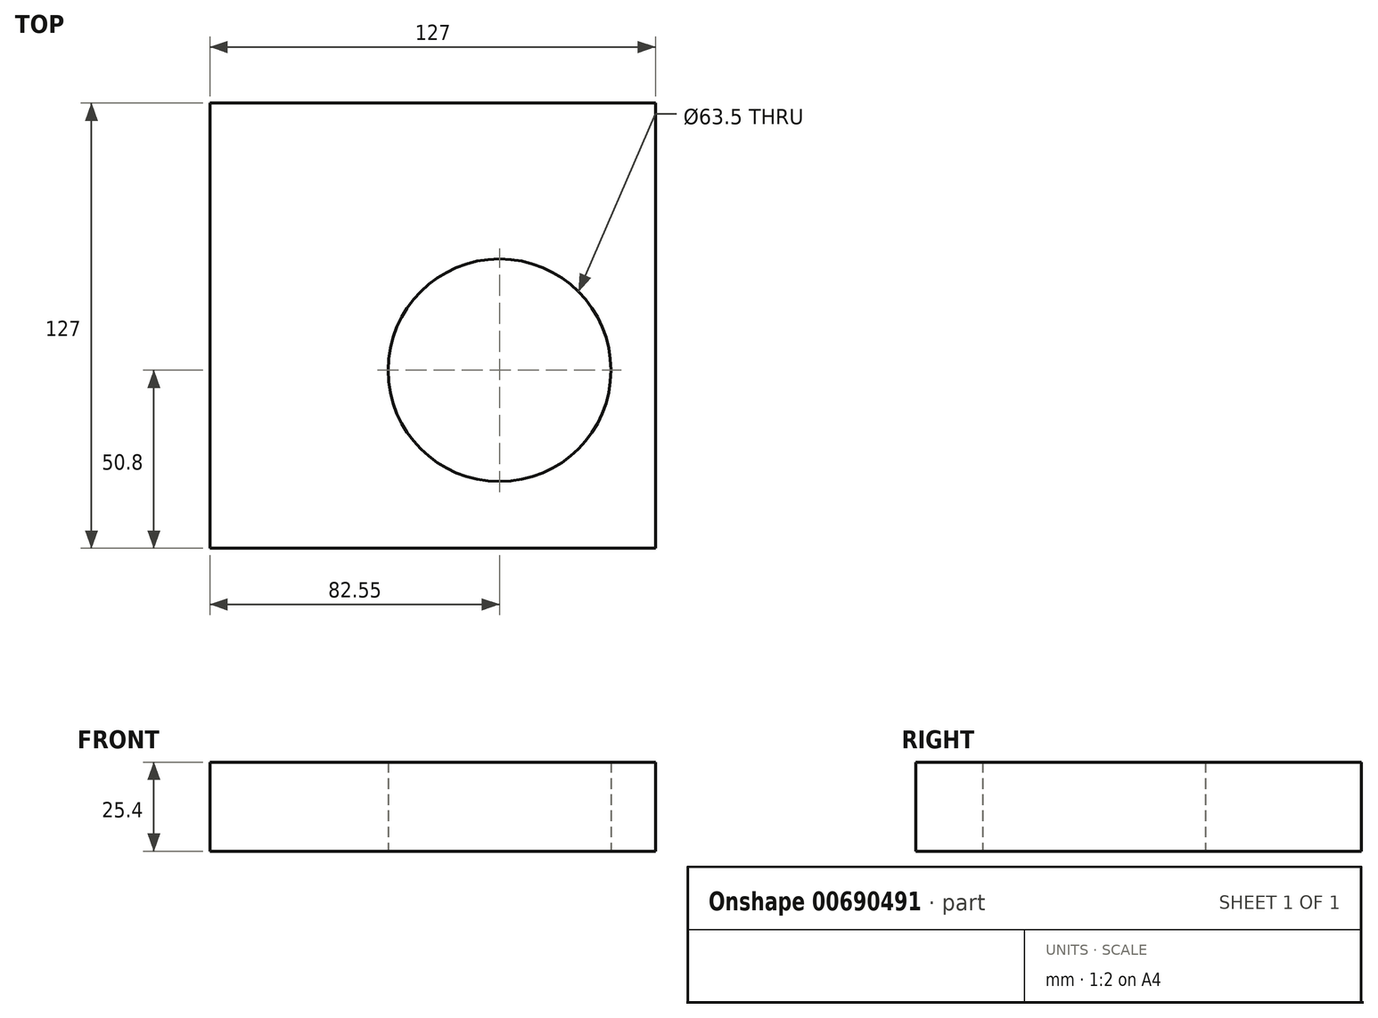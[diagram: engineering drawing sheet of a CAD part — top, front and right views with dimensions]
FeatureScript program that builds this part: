
annotation { "Feature Type Name" : "Feature", "Feature Type Description" : "" }
export const myFeature = defineFeature(function(context is Context, id is Id, definition is map)
    precondition{}
    {
        {
            var Q0;
            Q0=qCreatedBy(makeId("Top.planeOp"),FACE);
            var sketch = newSketch(context, id + "F0", { "sketchPlane" : qUnion([Q0])});
            skLineSegment(sketch, "E0.bottom", {"start": v(-63.5, -63.5) * mm, "end": v(63.5, -63.5) * mm});
            skLineSegment(sketch, "E0.top", {"start": v(-63.5, 63.5) * mm, "end": v(63.5, 63.5) * mm});
            skLineSegment(sketch, "E0.left", {"start": v(-63.5, -63.5) * mm, "end": v(-63.5, 63.5) * mm});
            skLineSegment(sketch, "E0.right", {"start": v(63.5, -63.5) * mm, "end": v(63.5, 63.5) * mm});
            skPoint(sketch, "E0.middle", {"position": v(0, 0) * mm});
            skCircle(sketch, "E1", {"center": v(19.05, -12.7) * mm, "radius": 31.75 * mm});
            skSolve(sketch);
        }
        {
            var Q0;
            Q0=makeQuery(id+"F0.imprint","IMPRINT",FACE,{"disambiguationData":[TD([[makeQuery(id+"F0.imprint","IMPRINT",EDGE,{"derivedFrom":sQuery(id+"F0.wireOp",EDGE,"E0.bottom")}),1.0]])]});
            extrude(context, id + "F1", {"entities" : qUnion([Q0]), "depth" : 50.8 * mm, "offsetDistance" : 25.4 * mm});
        }
        {
            var Q0;
            Q0=makeQuery(id+"F1.opExtrude","SWEPT_FACE",FACE,{"disambiguationData":[OSD([sQuery(id+"F0.wireOp",EDGE,"E0.bottom")])]});
            var sketch = newSketch(context, id + "F2", { "sketchPlane" : qUnion([Q0])});
            skLineSegment(sketch, "E2.bottom", {"start": v(-63.5, 0) * mm, "end": v(63.5, 0) * mm});
            skLineSegment(sketch, "E2.top", {"start": v(-63.5, 25.4) * mm, "end": v(63.5, 25.4) * mm});
            skLineSegment(sketch, "E2.left", {"start": v(-63.5, 0) * mm, "end": v(-63.5, 25.4) * mm});
            skLineSegment(sketch, "E2.right", {"start": v(63.5, 0) * mm, "end": v(63.5, 25.4) * mm});
            skSolve(sketch);
        }
        {
            var Q0;
            Q0=makeQuery(id+"F2.imprint","IMPRINT",FACE,{"disambiguationData":[TD([[makeQuery(id+"F2.imprint","IMPRINT",EDGE,{"derivedFrom":sQuery(id+"F2.wireOp",EDGE,"E2.bottom")}),1.0]])]});
            extrude(context, id + "F3", {"entities" : qUnion([Q0]), "operationType" : NewBodyOperationType.REMOVE, "oppositeDirection" : true, "depth" : 127 * mm, "offsetDistance" : 25.4 * mm});
        }
    });
